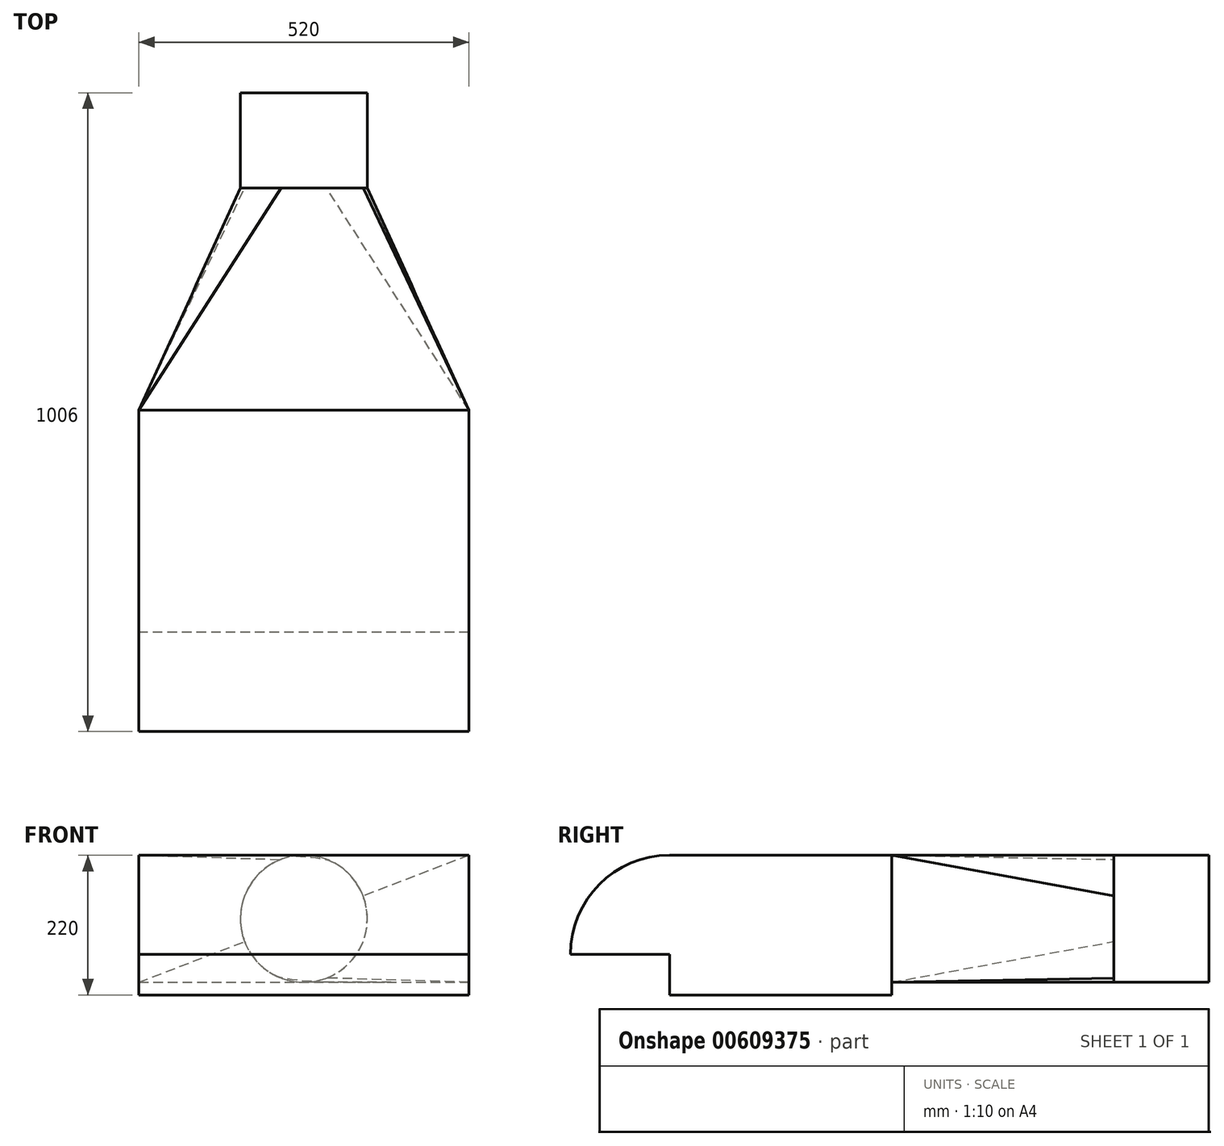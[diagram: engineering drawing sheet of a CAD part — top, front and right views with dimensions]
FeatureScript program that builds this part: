
annotation { "Feature Type Name" : "Feature", "Feature Type Description" : "" }
export const myFeature = defineFeature(function(context is Context, id is Id, definition is map)
    precondition{}
    {
        {
            var Q0;
            Q0=qCreatedBy(makeId("Front.planeOp"),FACE);
            var sketch = newSketch(context, id + "F0", { "sketchPlane" : qUnion([Q0])});
            skLineSegment(sketch, "E0.bottom", {"start": v(0, 0) * mm, "end": v(520, 0) * mm});
            skLineSegment(sketch, "E0.top", {"start": v(0, 200) * mm, "end": v(520, 200) * mm});
            skLineSegment(sketch, "E0.left", {"start": v(0, 0) * mm, "end": v(0, 200) * mm});
            skLineSegment(sketch, "E0.right", {"start": v(520, 0) * mm, "end": v(520, 200) * mm});
            skSolve(sketch);
        }
        {
            var Q0;
            Q0=qCreatedBy(makeId("Front.planeOp"),FACE);
            var Q1;
            Q1 = qBodyType(qCreatedBy(id + "F2" ,EDGE), BodyType.WIRE);
            cPlane(context, id + "F1", {"entities" : qUnion([Q0, Q1]), "cplaneType" : CPlaneType.OFFSET, "offset" : 350 * mm, "oppositeDirection" : true, "width" : 150 * mm, "height" : 150 * mm});
        }
        {
            var Q0;
            Q0=qCreatedBy(id+"F1.planeOp",FACE);
            var sketch = newSketch(context, id + "F2", { "sketchPlane" : qUnion([Q0])});
            skCircle(sketch, "E1", {"center": v(260, 100) * mm, "radius": 100 * mm});
            skSolve(sketch);
        }
        {
            var Q0;
            Q0=makeQuery(id+"F0.imprint","IMPRINT",FACE,{"disambiguationData":[TD([[makeQuery(id+"F0.imprint","IMPRINT",EDGE,{"derivedFrom":sQuery(id+"F0.wireOp",EDGE,"E0.bottom")}),1.0]])]});
            var Q1;
            Q1=makeQuery(id+"F2.imprint","IMPRINT",FACE,{"disambiguationData":[TD([[makeQuery(id+"F2.imprint","IMPRINT",EDGE,{"derivedFrom":sQuery(id+"F2.wireOp",EDGE,"E1")}),1.0]])]});
            loft(context, id + "F3", {"sheetProfilesArray" : [{ "sheetProfileEntities" : qUnion([Q0]) }, { "sheetProfileEntities" : qUnion([Q1]) }]});
        }
        {
            var Q0;
            Q0 = qSketchRegion(id + "F2", true);
            extrude(context, id + "F4", {"entities" : qUnion([Q0]), "oppositeDirection" : true, "depth" : 150 * mm, "offsetDistance" : 25 * mm});
        }
        {
            var Q0;
            Q0=qCreatedBy(makeId("Right.planeOp"),FACE);
            var sketch = newSketch(context, id + "F5", { "sketchPlane" : qUnion([Q0])});
            skLineSegment(sketch, "E2.bottom", {"start": v(0, -20) * mm, "end": v(-350, -20) * mm});
            skLineSegment(sketch, "E2.top", {"start": v(0, 200) * mm, "end": v(-350, 200) * mm});
            skLineSegment(sketch, "E2.left", {"start": v(0, -20) * mm, "end": v(0, 200) * mm});
            skLineSegment(sketch, "E2.right", {"start": v(-350, -20) * mm, "end": v(-350, 44) * mm});
            skArc(sketch, "E3", {"start": v(-350, 200) * mm, "mid": v(-460.3, 154.3) * mm, "end": v(-506, 44) * mm});
            skLineSegment(sketch, "E4", {"start": v(-506, 44) * mm, "end": v(-350, 44) * mm});
            skSolve(sketch);
        }
        {
            var Q0;
            Q0=makeQuery(id+"F5.imprint","IMPRINT",FACE,{"disambiguationData":[TD([[makeQuery(id+"F5.imprint","IMPRINT",EDGE,{"derivedFrom":sQuery(id+"F5.wireOp",EDGE,"E2.bottom")}),-1.0]])]});
            extrude(context, id + "F6", {"entities" : qUnion([Q0]), "operationType" : NewBodyOperationType.ADD, "depth" : 520 * mm, "offsetDistance" : 25 * mm});
        }
    });
